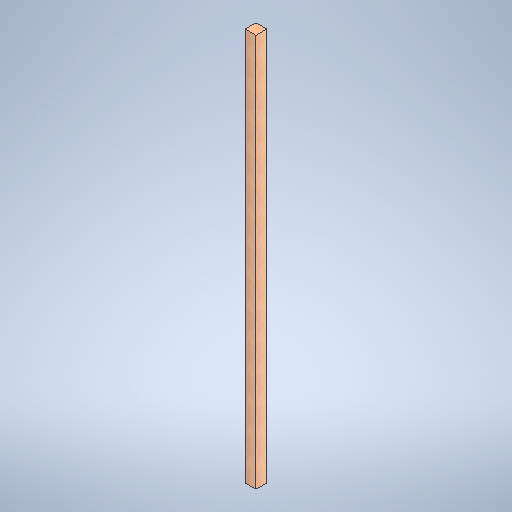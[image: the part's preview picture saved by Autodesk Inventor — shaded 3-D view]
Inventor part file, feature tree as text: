
AUTODESK INVENTOR PART (.ipt)
format: ipt  version: 2025 (Build 290162000, 162)  size: 279,040 bytes
history: native  units: in
note: dims shown in document units (in); Inventor stores cm internally (conversion verified against a paired STEP export)
features: extrude x1, sketch x1
ambient origin geometry x8: Origin, YZ Plane, XZ Plane, XY Plane, X Axis, Y Axis, Z Axis, Center Point
bodies: Solid1 (feature_tree)
feature tree (2):
  extrude  "Extrusion1"  Depth=4.0in
  sketch  "Sketch1"  dims[d0=4.0in d1=4.0in d2=144.0in d3=0.0in d4=0.5in d5=0.0344in d6=0.5in d7=0.0344in]
